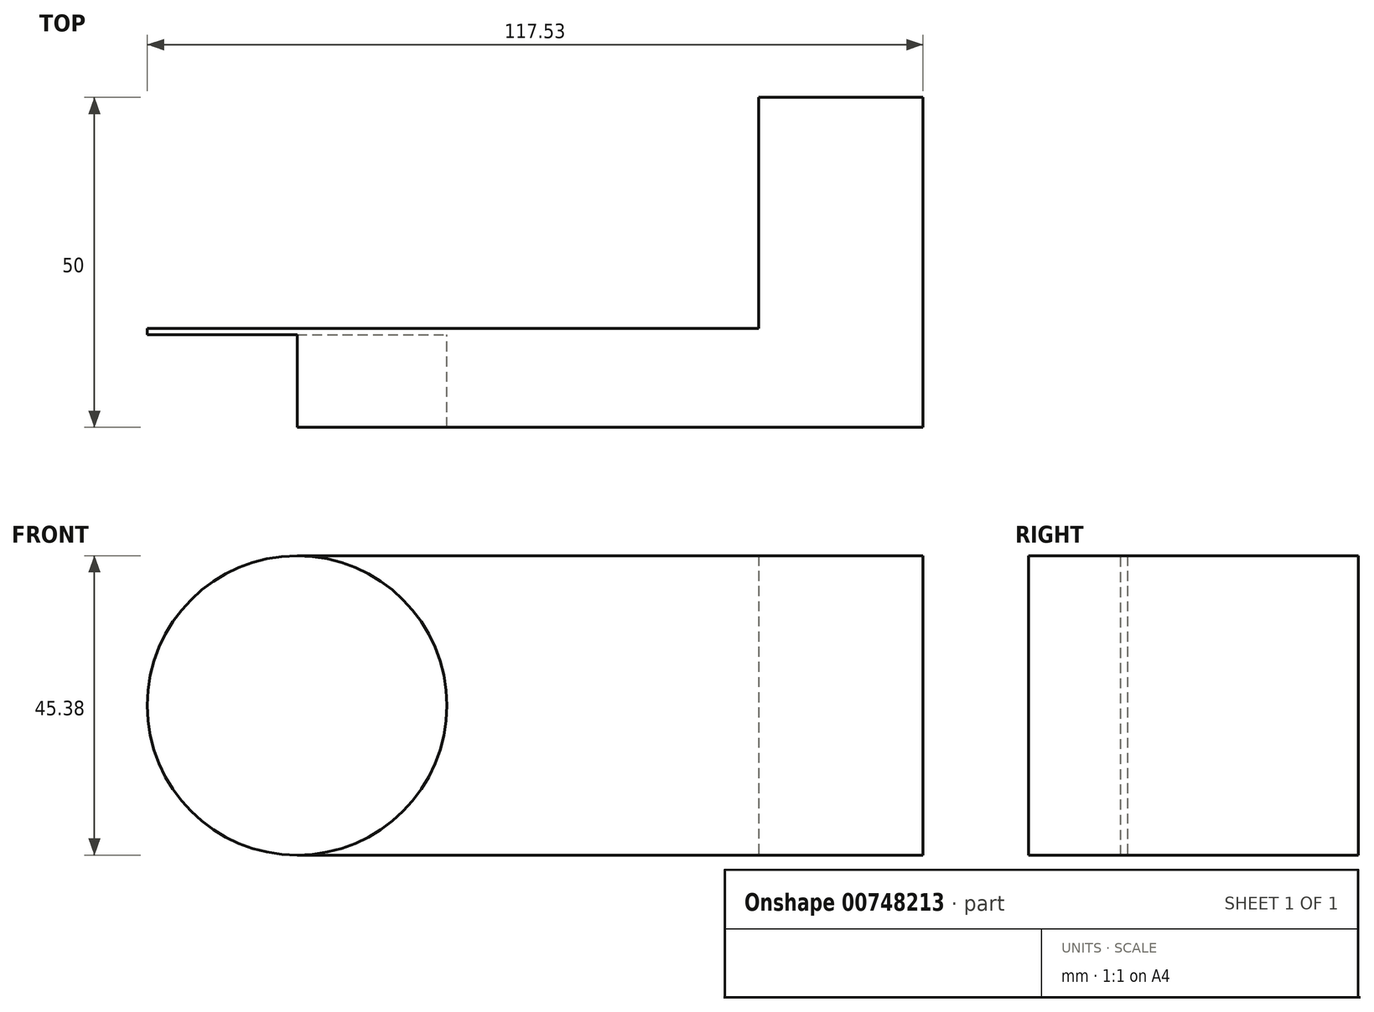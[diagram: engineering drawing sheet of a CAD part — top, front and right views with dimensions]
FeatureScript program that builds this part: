
annotation { "Feature Type Name" : "Feature", "Feature Type Description" : "" }
export const myFeature = defineFeature(function(context is Context, id is Id, definition is map)
    precondition{}
    {
        {
            var Q0;
            Q0=qCreatedBy(makeId("Front.planeOp"),FACE);
            var sketch = newSketch(context, id + "F0", { "sketchPlane" : qUnion([Q0])});
            skCircle(sketch, "E0", {"center": v(-58.77, 0) * mm, "radius": 22.7 * mm});
            skLineSegment(sketch, "E1.bottom", {"start": v(-58.77, 22.7) * mm, "end": v(36.07, 22.7) * mm});
            skLineSegment(sketch, "E1.top", {"start": v(-58.77, -22.7) * mm, "end": v(36.07, -22.7) * mm});
            skLineSegment(sketch, "E1.left", {"start": v(-58.77, 22.7) * mm, "end": v(-58.77, -22.7) * mm});
            skLineSegment(sketch, "E1.right", {"start": v(36.07, 22.7) * mm, "end": v(36.07, -22.7) * mm});
            skSolve(sketch);
        }
        {
            var Q0;
            Q0=sQuery(id+"F0.wireOp",EDGE,"E0");
            extrude(context, id + "F1", {"bodyType" : ToolBodyType.SURFACE, "surfaceEntities" : qUnion([Q0]), "depth" : 25 * mm, "offsetDistance" : 25 * mm});
        }
        {
            var Q0;
            {var subQ1=sQuery(id+"F0.wireOp",EDGE,"E1.bottom");Q0=makeQuery(id+"F0.imprint","IMPRINT",FACE,{"disambiguationData":[TD([[makeQuery(id+"F0.imprint","IMPRINT",EDGE,{"derivedFrom":subQ1}),-1.0]])]});}
            extrude(context, id + "F2", {"entities" : qUnion([Q0]), "depth" : 15 * mm, "offsetDistance" : 25 * mm});
        }
        {
            var Q0;
            Q0=makeQuery(id+"F2.opExtrude","CAP_FACE",FACE,{"disambiguationData":[OSD([sQuery(id+"F0.wireOp",EDGE,"E0"),sQuery(id+"F0.wireOp",EDGE,"E1.bottom"),sQuery(id+"F0.wireOp",EDGE,"E1.top"),sQuery(id+"F0.wireOp",EDGE,"E1.right")])],"isStart":false});
            var sketch = newSketch(context, id + "F3", { "sketchPlane" : qUnion([Q0])});
            skLineSegment(sketch, "E2.bottom", {"start": v(11.17, 22.7) * mm, "end": v(36.07, 22.7) * mm});
            skLineSegment(sketch, "E2.top", {"start": v(11.17, -22.7) * mm, "end": v(36.07, -22.7) * mm});
            skLineSegment(sketch, "E2.left", {"start": v(11.17, 22.7) * mm, "end": v(11.17, -22.7) * mm});
            skLineSegment(sketch, "E2.right", {"start": v(36.07, 22.7) * mm, "end": v(36.07, -22.7) * mm});
            skSolve(sketch);
        }
        {
            var Q0;
            Q0=makeQuery(id+"F3.imprint","IMPRINT",FACE,{"disambiguationData":[TD([[makeQuery(id+"F3.imprint","IMPRINT",EDGE,{"derivedFrom":sQuery(id+"F3.wireOp",EDGE,"E2.bottom")}),-1.0]])]});
            extrude(context, id + "F4", {"entities" : qUnion([Q0]), "operationType" : NewBodyOperationType.ADD, "oppositeDirection" : true, "depth" : 50 * mm, "offsetDistance" : 25 * mm});
        }
        {
            var Q0;
            {var subQ0=sQuery(id+"F0.wireOp",EDGE,"E1.left");Q0=makeQuery(id+"F0.imprint","IMPRINT",FACE,{"disambiguationData":[TD([[makeQuery(id+"F0.imprint","IMPRINT",EDGE,{"derivedFrom":subQ0}),1.0]])]});}
            var Q1;
            {var subQ0=sQuery(id+"F0.wireOp",EDGE,"E1.left");Q1=makeQuery(id+"F0.imprint","IMPRINT",FACE,{"disambiguationData":[TD([[makeQuery(id+"F0.imprint","IMPRINT",EDGE,{"derivedFrom":subQ0}),-1.0]])]});}
            extrude(context, id + "F5", {"entities" : qUnion([Q0, Q1]), "operationType" : NewBodyOperationType.ADD, "depth" : 1 * mm, "offsetDistance" : 25 * mm});
        }
    });
